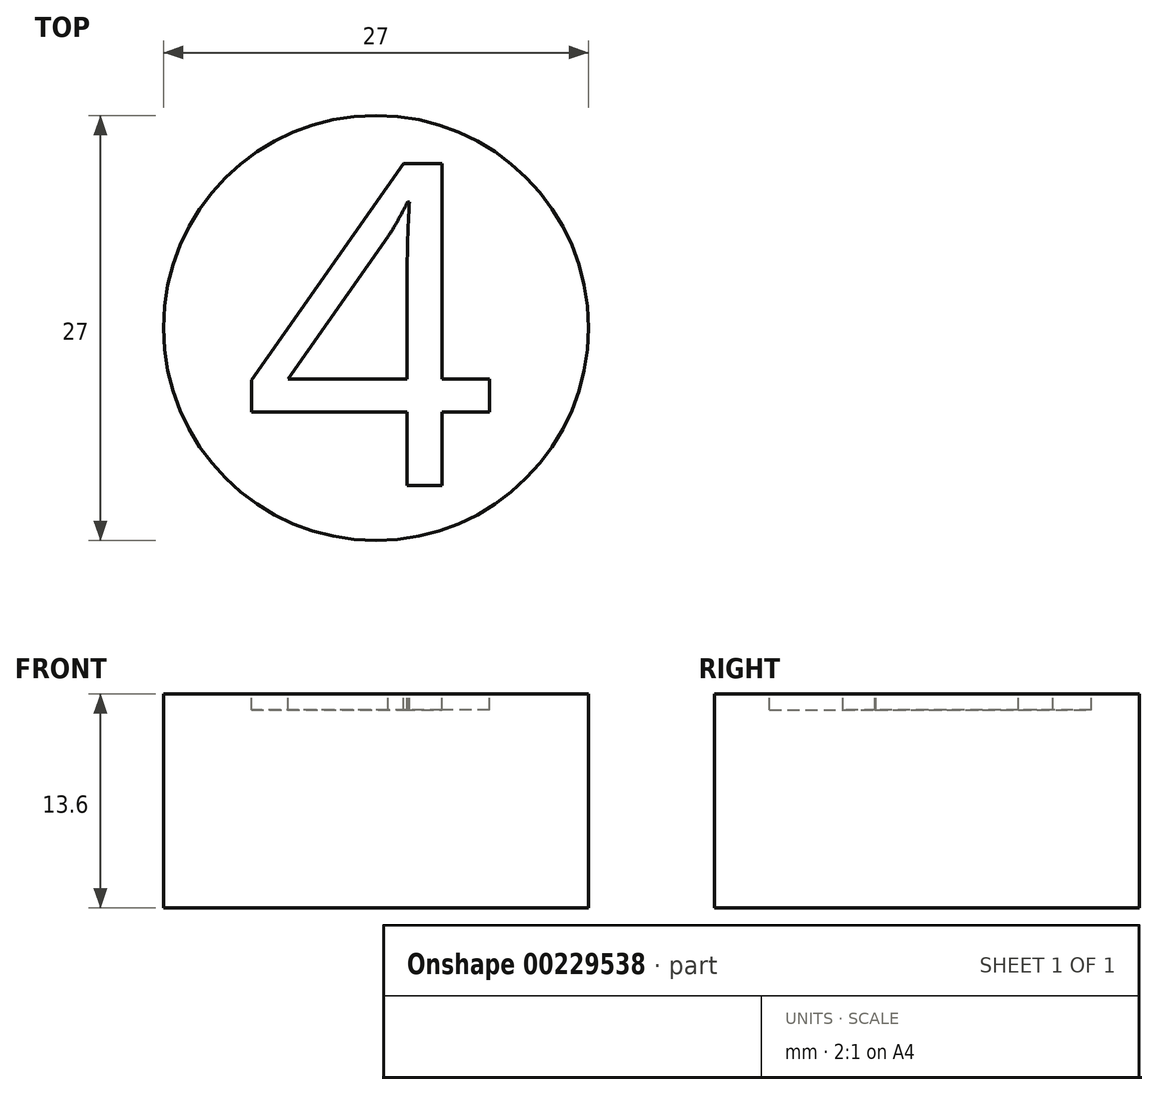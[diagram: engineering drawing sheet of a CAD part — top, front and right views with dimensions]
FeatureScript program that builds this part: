
annotation { "Feature Type Name" : "Feature", "Feature Type Description" : "" }
export const myFeature = defineFeature(function(context is Context, id is Id, definition is map)
    precondition{}
    {
        {
            var Q0;
            Q0=qCreatedBy(makeId("Top.planeOp"),FACE);
            var sketch = newSketch(context, id + "F0", { "sketchPlane" : qUnion([Q0])});
            skCircle(sketch, "E0", {"center": v(0, 0) * mm, "radius": 13.5 * mm});
            skSolve(sketch);
        }
        {
            var Q0;
            Q0=makeQuery(id+"F0.imprint","IMPRINT",FACE,{"disambiguationData":[TD([[makeQuery(id+"F0.imprint","IMPRINT",EDGE,{"derivedFrom":sQuery(id+"F0.wireOp",EDGE,"E0")}),1.0]])]});
            extrude(context, id + "F1", {"entities" : qUnion([Q0]), "depth" : 13.6 * mm});
        }
        {
            var Q0;
            Q0=makeQuery(id+"F1.opExtrude","CAP_FACE",FACE,{"disambiguationData":[OSD([sQuery(id+"F0.wireOp",EDGE,"E0")])],"isStart":false});
            var sketch = newSketch(context, id + "F2", { "sketchPlane" : qUnion([Q0])});
            skText(sketch, "E1", { "text": "4", "fontName": "OpenSans-Regular.ttf"});
            const initialGuessF2  = {"E1": [-0.0085, -0.01001, 1, 0, 0.0205]};
            skSetInitialGuess(sketch, initialGuessF2);
            skSolve(sketch);
        }
        {
            var Q0;
            Q0 = qSketchRegion(id + "F2", true);
            extrude(context, id + "F3", {"entities" : qUnion([Q0]), "operationType" : NewBodyOperationType.REMOVE, "oppositeDirection" : true, "depth" : 1 * mm});
        }
    });
